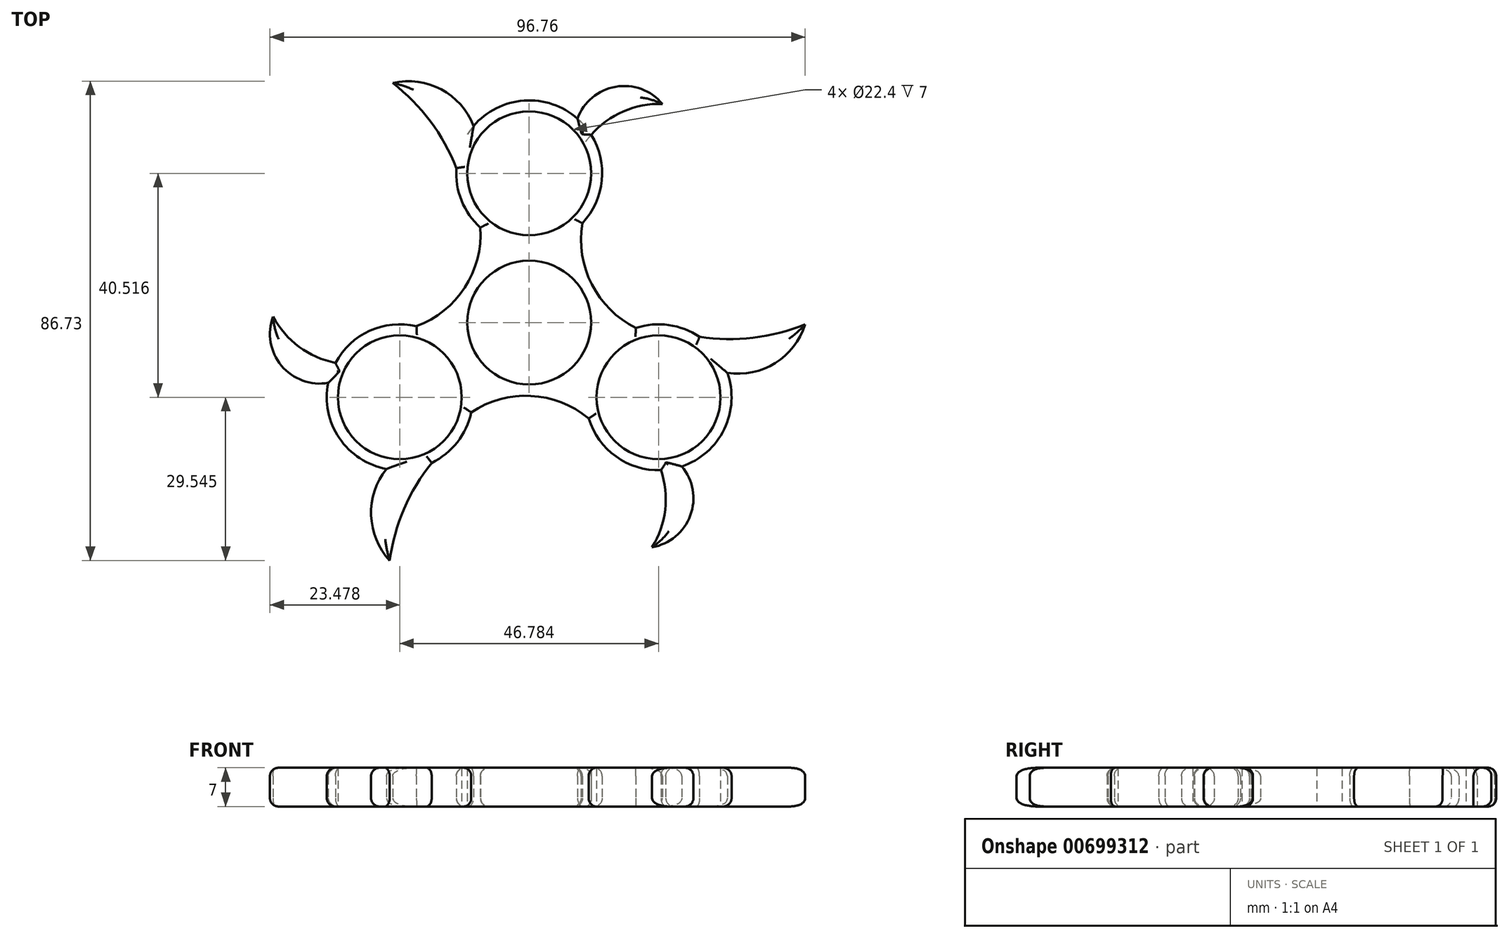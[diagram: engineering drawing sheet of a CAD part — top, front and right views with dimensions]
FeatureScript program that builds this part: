
annotation { "Feature Type Name" : "Feature", "Feature Type Description" : "" }
export const myFeature = defineFeature(function(context is Context, id is Id, definition is map)
    precondition{}
    {
        {
            var Q0;
            Q0=qCreatedBy(makeId("Top.planeOp"),FACE);
            var sketch = newSketch(context, id + "F0", { "sketchPlane" : qUnion([Q0])});
            skCircle(sketch, "E0", {"center": v(0, 0) * mm, "radius": 11.2 * mm});
            skCircle(sketch, "E1", {"center": v(0, 27.01) * mm, "radius": 11.2 * mm});
            skPoint(sketch, "E2.center.orphan", {"position": v(2.2, 27.01) * mm});
            skArc(sketch, "E3", {"start": v(9.63, 17.98) * mm, "mid": v(13.14, 25.71) * mm, "end": v(11.2, 33.99) * mm});
            skArc(sketch, "E4.1.0", {"start": v(-20.38, -0.65) * mm, "mid": v(-28.84, -1.48) * mm, "end": v(-35.04, -7.29) * mm});
            skCircle(sketch, "E4.1.1", {"center": v(-23.4, -13.5) * mm, "radius": 11.2 * mm});
            skArc(sketch, "E4.2.0", {"start": v(10.76, -17.33) * mm, "mid": v(15.7, -24.23) * mm, "end": v(23.83, -26.7) * mm});
            skCircle(sketch, "E4.2.1", {"center": v(23.4, -13.5) * mm, "radius": 11.2 * mm});
            skArc(sketch, "E5", {"start": v(24.1, 39.57) * mm, "mid": v(15.64, 42.68) * mm, "end": v(8.73, 36.91) * mm});
            skArc(sketch, "E6", {"start": v(24.1, 39.57) * mm, "mid": v(17.02, 38.22) * mm, "end": v(11.2, 33.99) * mm});
            skArc(sketch, "E7.1.0", {"start": v(-46.31, 1.08) * mm, "mid": v(-44.78, -7.8) * mm, "end": v(-36.33, -10.9) * mm});
            skArc(sketch, "E7.1.1", {"start": v(-46.31, 1.08) * mm, "mid": v(-41.6, -4.36) * mm, "end": v(-35.04, -7.29) * mm});
            skArc(sketch, "E7.2.0", {"start": v(22.22, -40.65) * mm, "mid": v(29.14, -34.89) * mm, "end": v(27.6, -26.02) * mm});
            skArc(sketch, "E7.2.1", {"start": v(22.22, -40.65) * mm, "mid": v(24.58, -33.85) * mm, "end": v(23.83, -26.7) * mm});
            skArc(sketch, "E8", {"start": v(-10.05, 35.57) * mm, "mid": v(-15.91, 42.2) * mm, "end": v(-24.67, 43.36) * mm});
            skArc(sketch, "E9", {"start": v(-13.17, 27.96) * mm, "mid": v(-17.88, 36.44) * mm, "end": v(-24.67, 43.36) * mm});
            skArc(sketch, "E10.1.0", {"start": v(-17.63, -25.38) * mm, "mid": v(-22.62, -33.7) * mm, "end": v(-25.22, -43.05) * mm});
            skArc(sketch, "E10.1.1", {"start": v(-25.78, -26.49) * mm, "mid": v(-28.58, -34.87) * mm, "end": v(-25.22, -43.05) * mm});
            skArc(sketch, "E10.2.0", {"start": v(30.8, -2.58) * mm, "mid": v(40.5, -2.74) * mm, "end": v(49.9, -0.31) * mm});
            skArc(sketch, "E10.2.1", {"start": v(35.83, -9.09) * mm, "mid": v(44.5, -7.32) * mm, "end": v(49.9, -0.31) * mm});
            skArc(sketch, "E11", {"start": v(9.63, 17.98) * mm, "mid": v(11.32, 6.9) * mm, "end": v(19.3, -0.96) * mm});
            skArc(sketch, "E12.1.0", {"start": v(-20.38, -0.65) * mm, "mid": v(-11.64, 6.35) * mm, "end": v(-8.82, 17.2) * mm});
            skArc(sketch, "E12.2.0", {"start": v(10.76, -17.33) * mm, "mid": v(0.32, -13.26) * mm, "end": v(-10.48, -16.24) * mm});
            skArc(sketch, "E13.trimOffspring", {"start": v(-17.63, -25.38) * mm, "mid": v(-13, -21.64) * mm, "end": v(-10.48, -16.24) * mm});
            skArc(sketch, "E14.trimOffspring", {"start": v(-36.33, -10.9) * mm, "mid": v(-34.32, -20.9) * mm, "end": v(-25.78, -26.49) * mm});
            skArc(sketch, "E15.trimOffspring", {"start": v(-13.17, 27.96) * mm, "mid": v(-12.24, 22.07) * mm, "end": v(-8.82, 17.2) * mm});
            skArc(sketch, "E16.trimOffspring", {"start": v(8.73, 36.91) * mm, "mid": v(-0.94, 40.18) * mm, "end": v(-10.05, 35.57) * mm});
            skArc(sketch, "E17.trimOffspring", {"start": v(30.8, -2.58) * mm, "mid": v(25.24, -0.43) * mm, "end": v(19.3, -0.96) * mm});
            skArc(sketch, "E18.trimOffspring", {"start": v(27.6, -26.02) * mm, "mid": v(35.26, -19.28) * mm, "end": v(35.83, -9.09) * mm});
            skSolve(sketch);
        }
        {
            var Q0;
            Q0=makeQuery(id+"F0.imprint","IMPRINT",FACE,{"disambiguationData":[TD([[makeQuery(id+"F0.imprint","IMPRINT",EDGE,{"derivedFrom":sQuery(id+"F0.wireOp",EDGE,"E0")}),-1.0]])]});
            extrude(context, id + "F1", {"entities" : qUnion([Q0]), "depth" : 7 * mm, "offsetDistance" : 25 * mm});
        }
        {
            var Q0;
            Q0=makeQuery(id+"F1.opExtrude","CAP_EDGE",EDGE,{"disambiguationData":[OSD([sQuery(id+"F0.wireOp",EDGE,"E12.2.0")])],"isStart":false});
            var Q1;
            Q1=makeQuery(id+"F1.opExtrude","CAP_EDGE",EDGE,{"disambiguationData":[OSD([sQuery(id+"F0.wireOp",EDGE,"E13.trimOffspring")])],"isStart":false});
            var Q2;
            Q2=makeQuery(id+"F1.opExtrude","CAP_EDGE",EDGE,{"disambiguationData":[OSD([sQuery(id+"F0.wireOp",EDGE,"E10.1.0")])],"isStart":false});
            var Q3;
            Q3=makeQuery(id+"F1.opExtrude","CAP_EDGE",EDGE,{"disambiguationData":[OSD([sQuery(id+"F0.wireOp",EDGE,"E10.1.1")])],"isStart":false});
            var Q4;
            Q4=makeQuery(id+"F1.opExtrude","CAP_EDGE",EDGE,{"disambiguationData":[OSD([sQuery(id+"F0.wireOp",EDGE,"E14.trimOffspring")])],"isStart":false});
            var Q5;
            Q5=makeQuery(id+"F1.opExtrude","CAP_EDGE",EDGE,{"disambiguationData":[OSD([sQuery(id+"F0.wireOp",EDGE,"E7.1.0")])],"isStart":false});
            var Q6;
            Q6=makeQuery(id+"F1.opExtrude","CAP_EDGE",EDGE,{"disambiguationData":[OSD([sQuery(id+"F0.wireOp",EDGE,"E12.1.0")])],"isStart":false});
            var Q7;
            Q7=makeQuery(id+"F1.opExtrude","CAP_EDGE",EDGE,{"disambiguationData":[OSD([sQuery(id+"F0.wireOp",EDGE,"E4.1.0")])],"isStart":false});
            var Q8;
            Q8=makeQuery(id+"F1.opExtrude","CAP_EDGE",EDGE,{"disambiguationData":[OSD([sQuery(id+"F0.wireOp",EDGE,"E7.1.1")])],"isStart":false});
            var Q9;
            Q9=makeQuery(id+"F1.opExtrude","CAP_EDGE",EDGE,{"disambiguationData":[OSD([sQuery(id+"F0.wireOp",EDGE,"E15.trimOffspring")])],"isStart":false});
            var Q10;
            Q10=makeQuery(id+"F1.opExtrude","CAP_EDGE",EDGE,{"disambiguationData":[OSD([sQuery(id+"F0.wireOp",EDGE,"E9")])],"isStart":false});
            var Q11;
            Q11=makeQuery(id+"F1.opExtrude","CAP_EDGE",EDGE,{"disambiguationData":[OSD([sQuery(id+"F0.wireOp",EDGE,"E8")])],"isStart":false});
            var Q12;
            Q12=makeQuery(id+"F1.opExtrude","CAP_EDGE",EDGE,{"disambiguationData":[OSD([sQuery(id+"F0.wireOp",EDGE,"E16.trimOffspring")])],"isStart":false});
            var Q13;
            Q13=makeQuery(id+"F1.opExtrude","CAP_EDGE",EDGE,{"disambiguationData":[OSD([sQuery(id+"F0.wireOp",EDGE,"E5")])],"isStart":false});
            var Q14;
            Q14=makeQuery(id+"F1.opExtrude","CAP_EDGE",EDGE,{"disambiguationData":[OSD([sQuery(id+"F0.wireOp",EDGE,"E6")])],"isStart":false});
            var Q15;
            Q15=makeQuery(id+"F1.opExtrude","CAP_EDGE",EDGE,{"disambiguationData":[OSD([sQuery(id+"F0.wireOp",EDGE,"E3")])],"isStart":false});
            var Q16;
            Q16=makeQuery(id+"F1.opExtrude","CAP_EDGE",EDGE,{"disambiguationData":[OSD([sQuery(id+"F0.wireOp",EDGE,"E11")])],"isStart":false});
            var Q17;
            Q17=makeQuery(id+"F1.opExtrude","CAP_EDGE",EDGE,{"disambiguationData":[OSD([sQuery(id+"F0.wireOp",EDGE,"E17.trimOffspring")])],"isStart":false});
            var Q18;
            Q18=makeQuery(id+"F1.opExtrude","CAP_EDGE",EDGE,{"disambiguationData":[OSD([sQuery(id+"F0.wireOp",EDGE,"E10.2.0")])],"isStart":false});
            var Q19;
            Q19=makeQuery(id+"F1.opExtrude","CAP_EDGE",EDGE,{"disambiguationData":[OSD([sQuery(id+"F0.wireOp",EDGE,"E10.2.1")])],"isStart":false});
            var Q20;
            Q20=makeQuery(id+"F1.opExtrude","CAP_EDGE",EDGE,{"disambiguationData":[OSD([sQuery(id+"F0.wireOp",EDGE,"E18.trimOffspring")])],"isStart":false});
            var Q21;
            Q21=makeQuery(id+"F1.opExtrude","CAP_EDGE",EDGE,{"disambiguationData":[OSD([sQuery(id+"F0.wireOp",EDGE,"E4.2.0")])],"isStart":false});
            var Q22;
            Q22=makeQuery(id+"F1.opExtrude","CAP_EDGE",EDGE,{"disambiguationData":[OSD([sQuery(id+"F0.wireOp",EDGE,"E7.2.1")])],"isStart":false});
            var Q23;
            Q23=makeQuery(id+"F1.opExtrude","CAP_EDGE",EDGE,{"disambiguationData":[OSD([sQuery(id+"F0.wireOp",EDGE,"E7.2.0")])],"isStart":false});
            fillet(context, id + "F2", {"entities" : qUnion([Q0, Q1, Q2, Q3, Q4, Q5, Q6, Q7, Q8, Q9, Q10, Q11, Q12, Q13, Q14, Q15, Q16, Q17, Q18, Q19, Q20, Q21, Q22, Q23]), "radius" : 1.5 * mm, "tangentPropagation" : true, "allowEdgeOverflow" : false});
        }
        {
            var Q0;
            Q0=makeQuery(id+"F1.opExtrude","CAP_EDGE",EDGE,{"disambiguationData":[OSD([sQuery(id+"F0.wireOp",EDGE,"E14.trimOffspring")])],"isStart":true});
            var Q1;
            Q1=makeQuery(id+"F1.opExtrude","CAP_EDGE",EDGE,{"disambiguationData":[OSD([sQuery(id+"F0.wireOp",EDGE,"E7.1.1")])],"isStart":true});
            var Q2;
            Q2=makeQuery(id+"F1.opExtrude","CAP_EDGE",EDGE,{"disambiguationData":[OSD([sQuery(id+"F0.wireOp",EDGE,"E7.1.0")])],"isStart":true});
            var Q3;
            Q3=makeQuery(id+"F1.opExtrude","CAP_EDGE",EDGE,{"disambiguationData":[OSD([sQuery(id+"F0.wireOp",EDGE,"E4.1.0")])],"isStart":true});
            var Q4;
            Q4=makeQuery(id+"F1.opExtrude","CAP_EDGE",EDGE,{"disambiguationData":[OSD([sQuery(id+"F0.wireOp",EDGE,"E12.1.0")])],"isStart":true});
            var Q5;
            Q5=makeQuery(id+"F1.opExtrude","CAP_EDGE",EDGE,{"disambiguationData":[OSD([sQuery(id+"F0.wireOp",EDGE,"E15.trimOffspring")])],"isStart":true});
            var Q6;
            Q6=makeQuery(id+"F1.opExtrude","CAP_EDGE",EDGE,{"disambiguationData":[OSD([sQuery(id+"F0.wireOp",EDGE,"E9")])],"isStart":true});
            var Q7;
            Q7=makeQuery(id+"F1.opExtrude","CAP_EDGE",EDGE,{"disambiguationData":[OSD([sQuery(id+"F0.wireOp",EDGE,"E8")])],"isStart":true});
            var Q8;
            Q8=makeQuery(id+"F1.opExtrude","CAP_EDGE",EDGE,{"disambiguationData":[OSD([sQuery(id+"F0.wireOp",EDGE,"E5")])],"isStart":true});
            var Q9;
            Q9=makeQuery(id+"F1.opExtrude","CAP_EDGE",EDGE,{"disambiguationData":[OSD([sQuery(id+"F0.wireOp",EDGE,"E3")])],"isStart":true});
            var Q10;
            Q10=makeQuery(id+"F1.opExtrude","CAP_EDGE",EDGE,{"disambiguationData":[OSD([sQuery(id+"F0.wireOp",EDGE,"E11")])],"isStart":true});
            var Q11;
            Q11=makeQuery(id+"F1.opExtrude","CAP_EDGE",EDGE,{"disambiguationData":[OSD([sQuery(id+"F0.wireOp",EDGE,"E17.trimOffspring")])],"isStart":true});
            var Q12;
            Q12=makeQuery(id+"F1.opExtrude","CAP_EDGE",EDGE,{"disambiguationData":[OSD([sQuery(id+"F0.wireOp",EDGE,"E10.2.0")])],"isStart":true});
            var Q13;
            Q13=makeQuery(id+"F1.opExtrude","CAP_EDGE",EDGE,{"disambiguationData":[OSD([sQuery(id+"F0.wireOp",EDGE,"E18.trimOffspring")])],"isStart":true});
            var Q14;
            Q14=makeQuery(id+"F1.opExtrude","CAP_EDGE",EDGE,{"disambiguationData":[OSD([sQuery(id+"F0.wireOp",EDGE,"E7.2.0")])],"isStart":true});
            var Q15;
            Q15=makeQuery(id+"F1.opExtrude","CAP_EDGE",EDGE,{"disambiguationData":[OSD([sQuery(id+"F0.wireOp",EDGE,"E10.2.1")])],"isStart":true});
            var Q16;
            Q16=makeQuery(id+"F1.opExtrude","CAP_EDGE",EDGE,{"disambiguationData":[OSD([sQuery(id+"F0.wireOp",EDGE,"E7.2.1")])],"isStart":true});
            var Q17;
            Q17=makeQuery(id+"F1.opExtrude","CAP_EDGE",EDGE,{"disambiguationData":[OSD([sQuery(id+"F0.wireOp",EDGE,"E4.2.0")])],"isStart":true});
            var Q18;
            Q18=makeQuery(id+"F1.opExtrude","CAP_EDGE",EDGE,{"disambiguationData":[OSD([sQuery(id+"F0.wireOp",EDGE,"E12.2.0")])],"isStart":true});
            var Q19;
            Q19=makeQuery(id+"F1.opExtrude","CAP_EDGE",EDGE,{"disambiguationData":[OSD([sQuery(id+"F0.wireOp",EDGE,"E13.trimOffspring")])],"isStart":true});
            var Q20;
            Q20=makeQuery(id+"F1.opExtrude","CAP_EDGE",EDGE,{"disambiguationData":[OSD([sQuery(id+"F0.wireOp",EDGE,"E10.1.0")])],"isStart":true});
            var Q21;
            Q21=makeQuery(id+"F1.opExtrude","CAP_EDGE",EDGE,{"disambiguationData":[OSD([sQuery(id+"F0.wireOp",EDGE,"E10.1.1")])],"isStart":true});
            fillet(context, id + "F3", {"entities" : qUnion([Q0, Q1, Q2, Q3, Q4, Q5, Q6, Q7, Q8, Q9, Q10, Q11, Q12, Q13, Q14, Q15, Q16, Q17, Q18, Q19, Q20, Q21]), "radius" : 1.5 * mm, "tangentPropagation" : true, "allowEdgeOverflow" : false});
        }
    });
